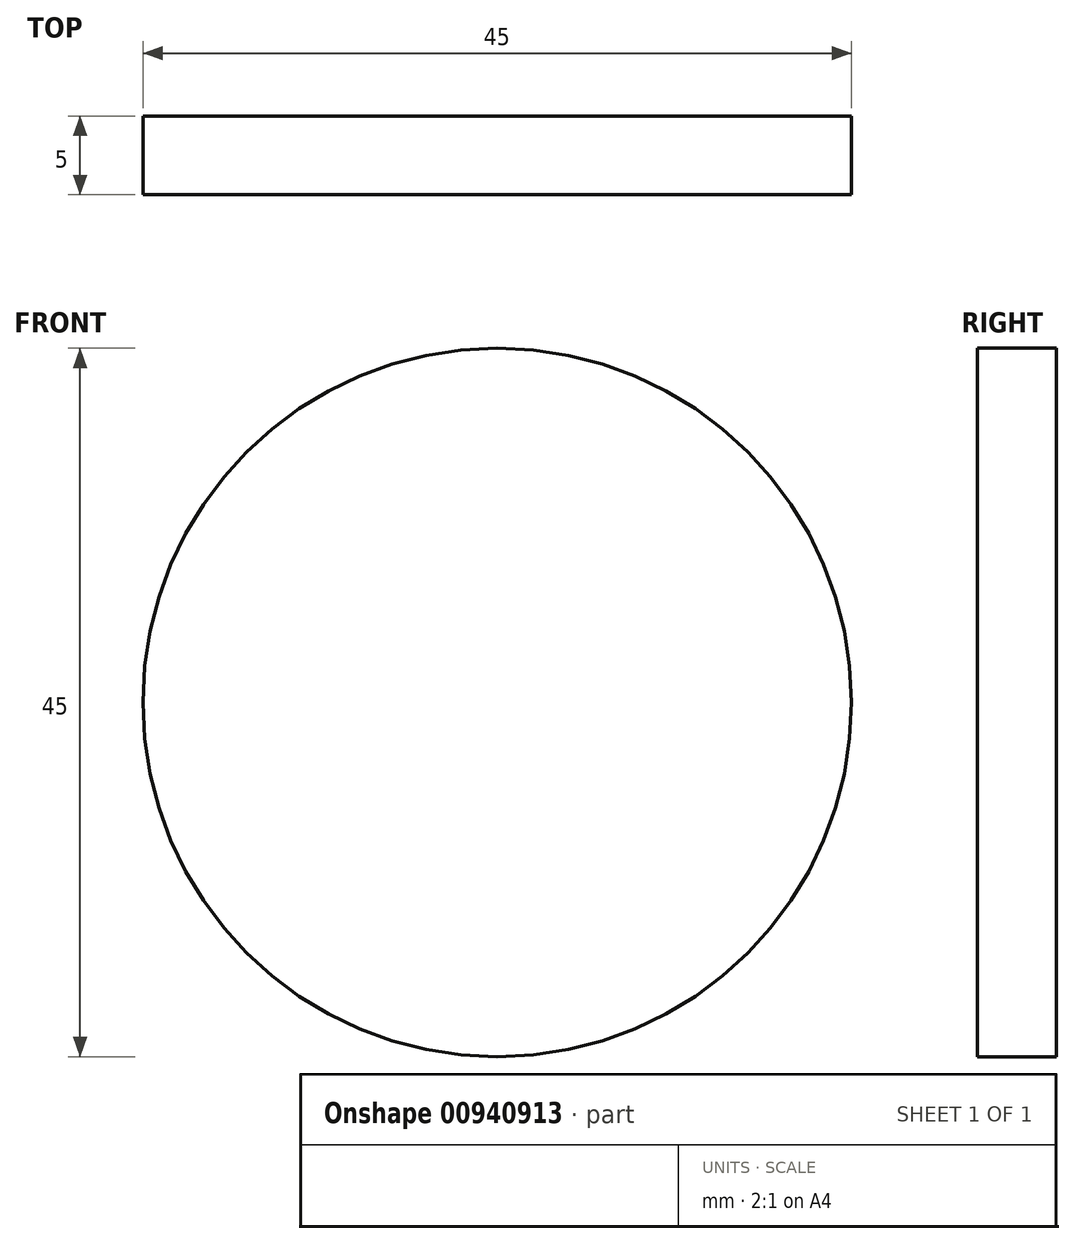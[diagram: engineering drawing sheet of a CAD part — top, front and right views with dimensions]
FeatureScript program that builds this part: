
annotation { "Feature Type Name" : "Feature", "Feature Type Description" : "" }
export const myFeature = defineFeature(function(context is Context, id is Id, definition is map)
    precondition{}
    {
        {
            var Q0;
            Q0=qCreatedBy(makeId("Front.planeOp"),FACE);
            var sketch = newSketch(context, id + "F0", { "sketchPlane" : qUnion([Q0])});
            skCircle(sketch, "E0", {"center": v(0, 0) * mm, "radius": 22.5 * mm});
            skSolve(sketch);
        }
        {
            var Q0;
            Q0 = qSketchRegion(id + "F0", true);
            extrude(context, id + "F1", {"entities" : qUnion([Q0]), "endBound" : BoundingType.SYMMETRIC, "depth" : 5 * mm, "offsetDistance" : 25 * mm});
        }
    });
